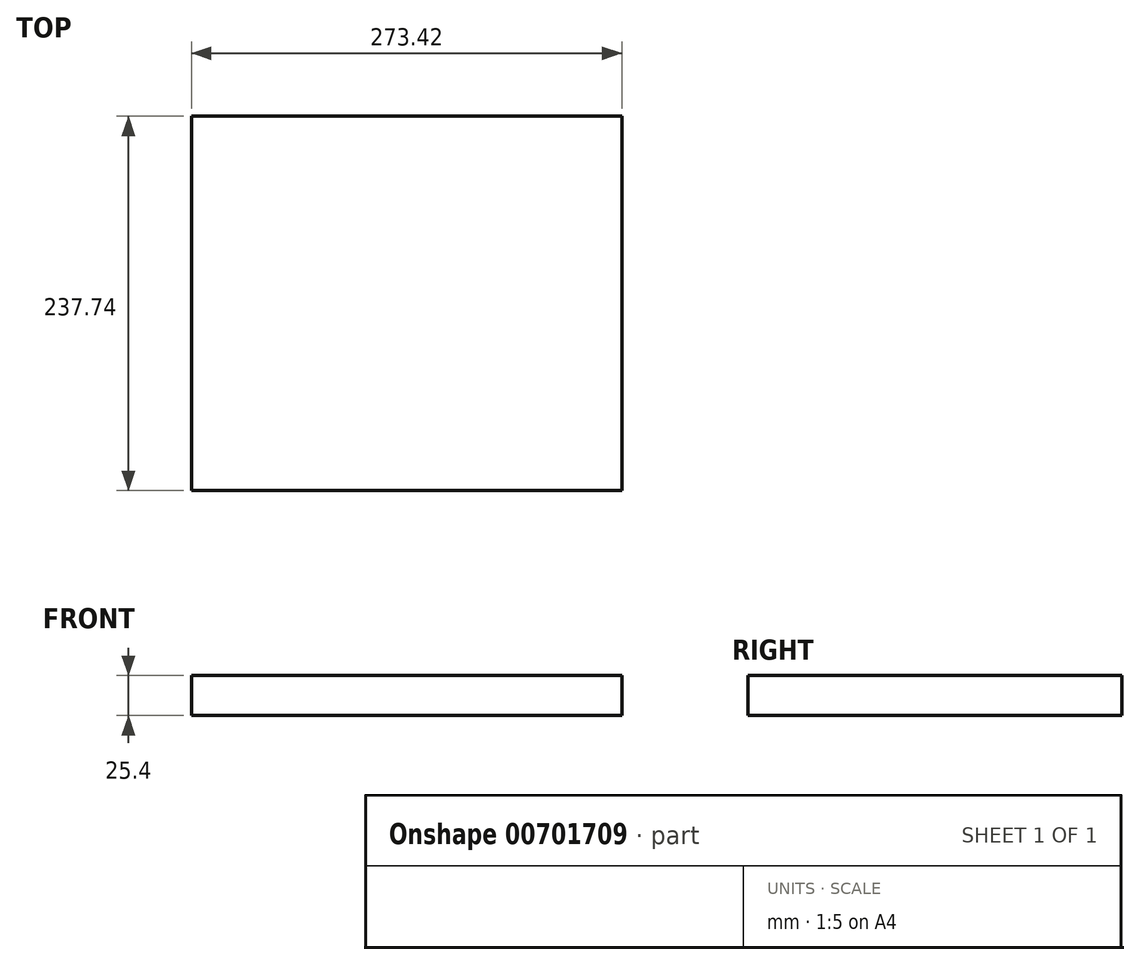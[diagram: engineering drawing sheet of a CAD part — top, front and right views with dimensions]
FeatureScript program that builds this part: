
annotation { "Feature Type Name" : "Feature", "Feature Type Description" : "" }
export const myFeature = defineFeature(function(context is Context, id is Id, definition is map)
    precondition{}
    {
        {
            var Q0;
            Q0=qCreatedBy(makeId("Front.planeOp"),FACE);
            var sketch = newSketch(context, id + "F0", { "sketchPlane" : qUnion([Q0])});
            skLineSegment(sketch, "E0", {"start": v(-149.24, 9.7) * mm, "end": v(-149.24, -15.7) * mm});
            skLineSegment(sketch, "E1", {"start": v(-149.24, -15.7) * mm, "end": v(124.18, -15.7) * mm});
            skLineSegment(sketch, "E2", {"start": v(124.18, -15.7) * mm, "end": v(124.18, 9.7) * mm});
            skLineSegment(sketch, "E3", {"start": v(124.18, 9.7) * mm, "end": v(-149.24, 9.7) * mm});
            skLineSegment(sketch, "E4.bottom", {"start": v(81.3, 111.3) * mm, "end": v(158.58, 111.3) * mm});
            skLineSegment(sketch, "E4.top", {"start": v(81.3, 9.7) * mm, "end": v(158.58, 9.7) * mm});
            skLineSegment(sketch, "E4.left", {"start": v(81.3, 111.3) * mm, "end": v(81.3, 9.7) * mm});
            skLineSegment(sketch, "E4.right", {"start": v(158.58, 111.3) * mm, "end": v(158.58, 9.7) * mm});
            skLineSegment(sketch, "E5.bottom", {"start": v(158.58, 111.3) * mm, "end": v(231.7, 111.3) * mm});
            skLineSegment(sketch, "E5.top", {"start": v(158.58, 48.31) * mm, "end": v(231.7, 48.31) * mm});
            skLineSegment(sketch, "E5.left", {"start": v(158.58, 111.3) * mm, "end": v(158.58, 48.31) * mm});
            skLineSegment(sketch, "E5.right", {"start": v(231.7, 111.3) * mm, "end": v(231.7, 48.31) * mm});
            skFitSpline(sketch, "E6", {"points": [v(-149.24, 9.7) * mm, v(81.3, 111.3) * mm], "startDerivative": vector(129.26, 153.42) * mm, "endDerivative": vector(258.8, 4.26) * mm});
            skSolve(sketch);
        }
        {
            var Q0;
            Q0=makeQuery(id+"F0.imprint","IMPRINT",FACE,{"disambiguationData":[TD([[makeQuery(id+"F0.imprint","IMPRINT",EDGE,{"derivedFrom":sQuery(id+"F0.wireOp",EDGE,"E0")}),1.0]])]});
            extrude(context, id + "F1", {"entities" : qUnion([Q0]), "endBound" : BoundingType.SYMMETRIC, "depth" : 237.74 * mm, "offsetDistance" : 25.4 * mm});
        }
    });
